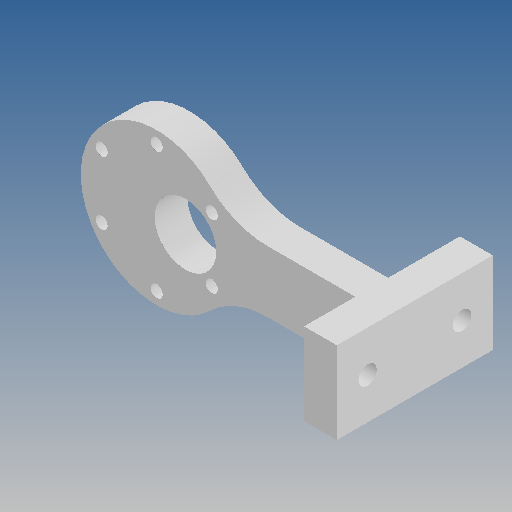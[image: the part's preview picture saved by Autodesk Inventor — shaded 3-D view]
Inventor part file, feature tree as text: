
AUTODESK INVENTOR PART (.ipt)
format: ipt  version: 2021 (Build 250183000, 183)  size: 147,968 bytes
history: native  units: mm
features: other x3, extrude x2, sketch x2, fillet x1, reference x1
ambient origin geometry x8: Origin, YZ Plane, XZ Plane, XY Plane, X Axis, Y Axis, Z Axis, Center Point
bodies: Solid1 (feature_tree)
feature tree (9):
  extrude  "Extrusion1"  Depth=15.0mm
  extrude  "Extrusion2"  Depth=7.0mm
  fillet  "Fillet1"  Radius=2.5mm
  sketch  "Sketch1"  dims[d0=15.0mm d1=35.0mm]
  reference  "Reference1"
  sketch  "Sketch2"  dims[d2=20.0mm d3=7.0mm d4=2.5mm d5=0.0mm d6=8.0mm d7=0.0mm d8=20.0mm d9=0.0mm d10=38.0mm d11=15.0mm d12=4.5mm d13=4.5mm d14=7.5mm d15=7.5mm d16=8.0mm d17=0.0mm d18=20.0mm]
  other  "<userpath>\OneDrive\Objet3D\3DPrinter\3DPrinterBeltCoreXY.iam"
  other  "3DPrinterBeltCoreXY.iam"
  other  "DCMotor:1"
